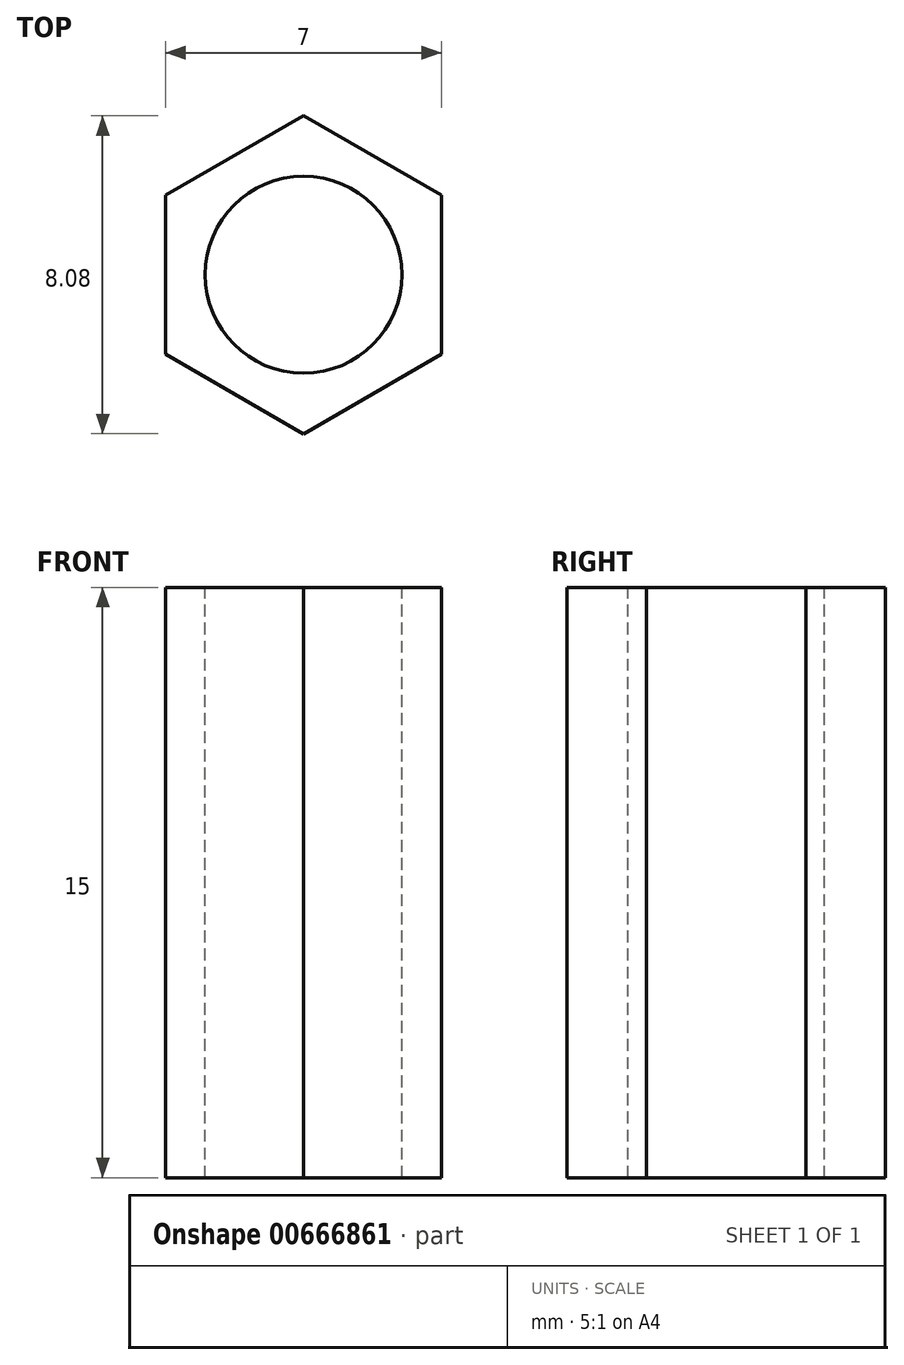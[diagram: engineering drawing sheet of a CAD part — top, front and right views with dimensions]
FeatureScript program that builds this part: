
annotation { "Feature Type Name" : "Feature", "Feature Type Description" : "" }
export const myFeature = defineFeature(function(context is Context, id is Id, definition is map)
    precondition{}
    {
        {
            var Q0;
            Q0=qCreatedBy(makeId("Top.planeOp"),FACE);
            var sketch = newSketch(context, id + "F0", { "sketchPlane" : qUnion([Q0])});
            skCircle(sketch, "E0.cCircle", {"center": v(0, 0) * mm, "radius": 3.5 * mm, "construction": true});
            skLineSegment(sketch, "E0.0", {"start": v(3.5, 2.02) * mm, "end": v(3.5, -2.02) * mm});
            skLineSegment(sketch, "E0.1", {"start": v(3.5, -2.02) * mm, "end": v(0, -4.04) * mm});
            skLineSegment(sketch, "E0.2", {"start": v(0, -4.04) * mm, "end": v(-3.5, -2.02) * mm});
            skLineSegment(sketch, "E0.3", {"start": v(-3.5, -2.02) * mm, "end": v(-3.5, 2.02) * mm});
            skLineSegment(sketch, "E0.4", {"start": v(-3.5, 2.02) * mm, "end": v(0, 4.04) * mm});
            skLineSegment(sketch, "E0.5", {"start": v(0, 4.04) * mm, "end": v(3.5, 2.02) * mm});
            skPoint(sketch, "E0.0.midPoint", {"position": v(3.5, 0) * mm});
            skSolve(sketch);
        }
        {
            var Q0;
            Q0 = qSketchRegion(id + "F0", true);
            extrude(context, id + "F1", {"entities" : qUnion([Q0]), "depth" : 15 * mm, "offsetDistance" : 25 * mm});
        }
        {
            var Q0;
            Q0=makeQuery(id+"F1.opExtrude","CAP_FACE",FACE,{"disambiguationData":[OSD([sQuery(id+"F0.wireOp",EDGE,"E0.0"),sQuery(id+"F0.wireOp",EDGE,"E0.1"),sQuery(id+"F0.wireOp",EDGE,"E0.2"),sQuery(id+"F0.wireOp",EDGE,"E0.3"),sQuery(id+"F0.wireOp",EDGE,"E0.4"),sQuery(id+"F0.wireOp",EDGE,"E0.5")])],"isStart":false});
            var sketch = newSketch(context, id + "F2", { "sketchPlane" : qUnion([Q0])});
            skCircle(sketch, "E1", {"center": v(0, 0) * mm, "radius": 2.5 * mm});
            skSolve(sketch);
        }
        {
            var Q0;
            Q0=makeQuery(id+"F2.imprint","IMPRINT",FACE,{"disambiguationData":[TD([[makeQuery(id+"F2.imprint","IMPRINT",EDGE,{"derivedFrom":sQuery(id+"F2.wireOp",EDGE,"E1")}),1.0]])]});
            extrude(context, id + "F3", {"entities" : qUnion([Q0]), "operationType" : NewBodyOperationType.REMOVE, "oppositeDirection" : true, "depth" : 25 * mm, "offsetDistance" : 25 * mm});
        }
    });
